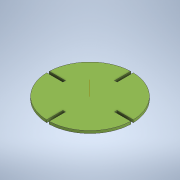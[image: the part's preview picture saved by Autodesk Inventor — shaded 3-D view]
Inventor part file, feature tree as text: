
AUTODESK INVENTOR PART (.ipt)
format: ipt  version: 2021 (Build 250183000, 183)  size: 136,704 bytes
history: native  units: in
note: dims shown in document units (in); Inventor stores cm internally (conversion verified against a paired STEP export)
features: sketch x2, extrude x1, other x1
ambient origin geometry x8: Origin, YZ Plane, XZ Plane, XY Plane, X Axis, Y Axis, Z Axis, Center Point
bodies: Solid1 (feature_tree)
feature tree (4):
  sketch  "Sketch1"  dims[d2=0.0315in d3=0.0315in]
  extrude  "Extrusion1"  Depth=0.0315in
  other  "Work Axis1"
  sketch  "Sketch2"  dims[d4=0.0315in d5=0.0315in d6=1.2598in d7=0.0in d8=0.0in d9=2.0472in d10=0.0in d11=0.0in d12=0.0in d13=0.063in d14=0.0in]
